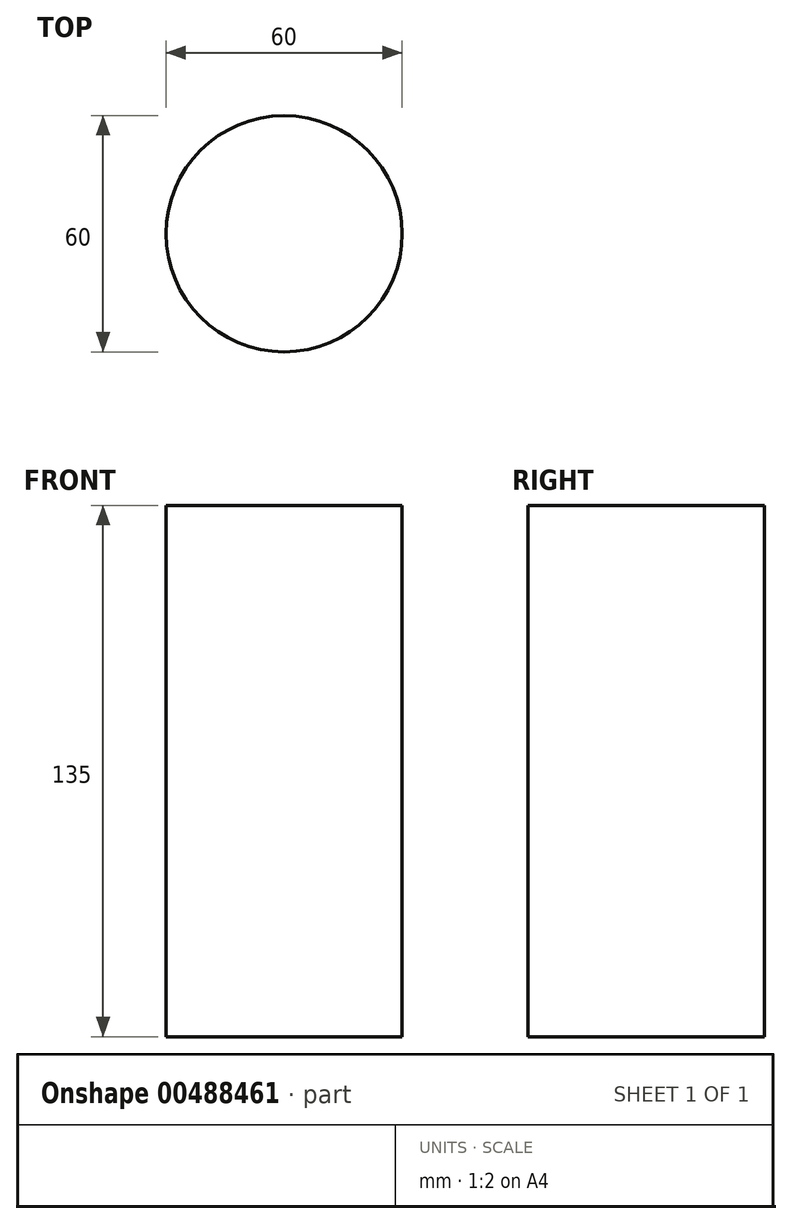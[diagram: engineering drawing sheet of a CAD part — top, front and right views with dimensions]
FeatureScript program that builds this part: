
annotation { "Feature Type Name" : "Feature", "Feature Type Description" : "" }
export const myFeature = defineFeature(function(context is Context, id is Id, definition is map)
    precondition{}
    {
        {
            var Q0;
            Q0=qCreatedBy(makeId("Top.planeOp"),FACE);
            var sketch = newSketch(context, id + "F0", { "sketchPlane" : qUnion([Q0])});
            skCircle(sketch, "E0", {"center": v(0, 0) * mm, "radius": 30 * mm});
            skSolve(sketch);
        }
        {
            var Q0;
            Q0 = qSketchRegion(id + "F0", true);
            extrude(context, id + "F1", {"entities" : qUnion([Q0]), "depth" : (110 + 25) * mm});
        }
    });
